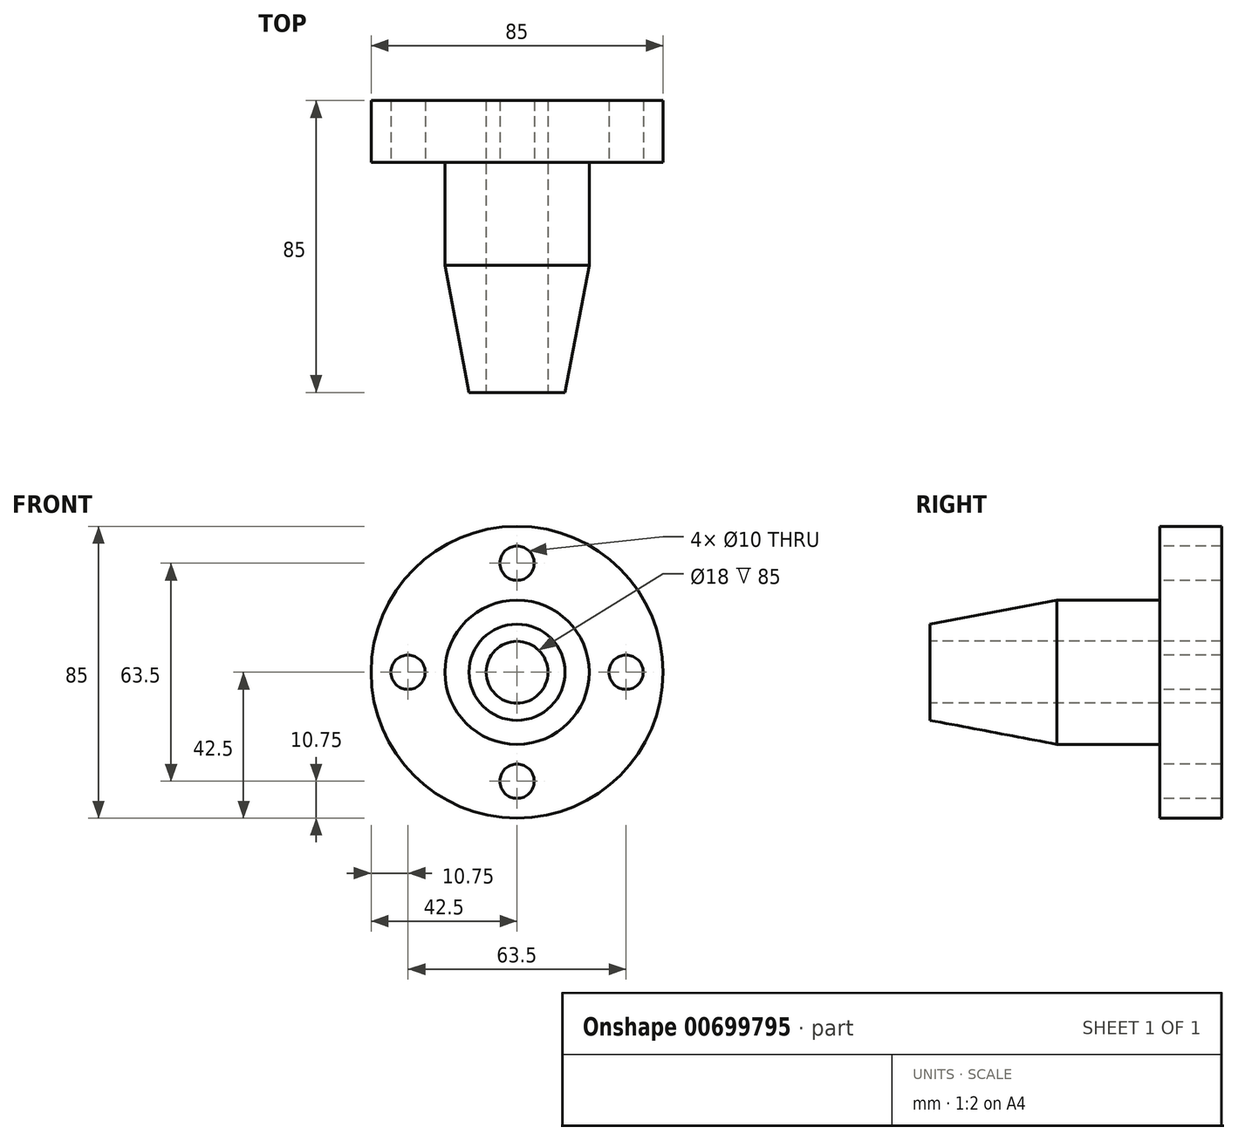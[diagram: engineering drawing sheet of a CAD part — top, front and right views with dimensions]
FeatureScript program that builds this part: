
annotation { "Feature Type Name" : "Feature", "Feature Type Description" : "" }
export const myFeature = defineFeature(function(context is Context, id is Id, definition is map)
    precondition{}
    {
        {
            var Q0;
            Q0=qCreatedBy(makeId("Top.planeOp"),FACE);
            var sketch = newSketch(context, id + "F0", { "sketchPlane" : qUnion([Q0])});
            skLineSegment(sketch, "E0", {"start": v(0, -104.11) * mm, "end": v(0, 87.37) * mm, "construction": true});
            skLineSegment(sketch, "E1", {"start": v(9, 43.82) * mm, "end": v(9, -41.18) * mm});
            skLineSegment(sketch, "E2", {"start": v(9, -41.18) * mm, "end": v(14, -41.18) * mm});
            skLineSegment(sketch, "E3", {"start": v(0, 43.82) * mm, "end": v(42.5, 43.82) * mm, "construction": true});
            skLineSegment(sketch, "E4", {"start": v(9, 43.82) * mm, "end": v(42.5, 43.82) * mm});
            skLineSegment(sketch, "E5", {"start": v(42.5, 43.82) * mm, "end": v(42.5, 25.82) * mm});
            skLineSegment(sketch, "E6", {"start": v(0, 25.82) * mm, "end": v(21, 25.82) * mm, "construction": true});
            skLineSegment(sketch, "E7", {"start": v(42.5, 25.82) * mm, "end": v(21, 25.82) * mm});
            skLineSegment(sketch, "E8", {"start": v(21, 25.82) * mm, "end": v(21, -4.18) * mm});
            skLineSegment(sketch, "E9", {"start": v(14, -41.18) * mm, "end": v(21, -4.18) * mm});
            skSolve(sketch);
        }
        {
            var Q0;
            Q0=makeQuery(id+"F0.imprint","IMPRINT",FACE,{"disambiguationData":[TD([[makeQuery(id+"F0.imprint","IMPRINT",EDGE,{"derivedFrom":sQuery(id+"F0.wireOp",EDGE,"E1")}),1.0]])]});
            var Q1;
            Q1=sQuery(id+"F0.wireOp",EDGE,"E0");
            revolve(context, id + "F1", {"entities" : qUnion([Q0]), "axis" : qUnion([Q1]), "revolveType" : RevolveType.FULL});
        }
        {
            var Q0;
            Q0=makeQuery(id+"F1.opRevolve","SWEPT_FACE",FACE,{"disambiguationData":[OSD([sQuery(id+"F0.wireOp",EDGE,"E7")])]});
            var sketch = newSketch(context, id + "F2", { "sketchPlane" : qUnion([Q0])});
            skLineSegment(sketch, "E10", {"start": v(0, 21) * mm, "end": v(0, 42.5) * mm, "construction": true});
            skLineSegment(sketch, "E11", {"start": v(-21, 0) * mm, "end": v(-42.5, 0) * mm, "construction": true});
            skLineSegment(sketch, "E12", {"start": v(0, -21) * mm, "end": v(0, -42.5) * mm, "construction": true});
            skLineSegment(sketch, "E13", {"start": v(21, 0) * mm, "end": v(42.5, 0) * mm, "construction": true});
            skCircle(sketch, "E14", {"center": v(0, 31.75) * mm, "radius": 5 * mm});
            skCircle(sketch, "E15", {"center": v(-31.75, 0) * mm, "radius": 5 * mm});
            skCircle(sketch, "E16", {"center": v(0, -31.75) * mm, "radius": 5 * mm});
            skCircle(sketch, "E17", {"center": v(31.75, 0) * mm, "radius": 5 * mm});
            skSolve(sketch);
        }
        {
            var Q0;
            Q0 = qSketchRegion(id + "F2", true);
            extrude(context, id + "F3", {"entities" : qUnion([Q0]), "operationType" : NewBodyOperationType.REMOVE, "endBound" : BoundingType.THROUGH_ALL, "oppositeDirection" : true, "depth" : 25 * mm, "offsetDistance" : 25 * mm});
        }
    });
